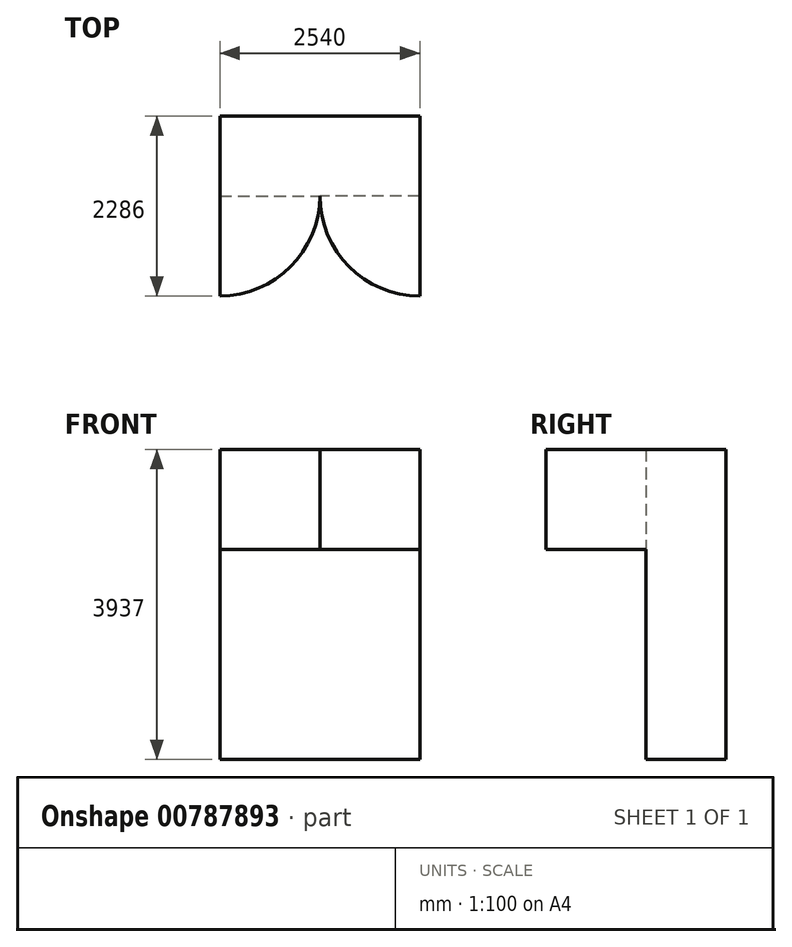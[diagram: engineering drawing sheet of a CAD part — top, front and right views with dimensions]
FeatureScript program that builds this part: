
annotation { "Feature Type Name" : "Feature", "Feature Type Description" : "" }
export const myFeature = defineFeature(function(context is Context, id is Id, definition is map)
    precondition{}
    {
        {
            var Q0;
            Q0=qCreatedBy(makeId("Top.planeOp"),FACE);
            var sketch = newSketch(context, id + "F0", { "sketchPlane" : qUnion([Q0])});
            skLineSegment(sketch, "E0.bottom", {"start": v(0, 0) * mm, "end": v(2540, 0) * mm});
            skLineSegment(sketch, "E0.top", {"start": v(0, 1016) * mm, "end": v(2540, 1016) * mm});
            skLineSegment(sketch, "E0.left", {"start": v(0, 0) * mm, "end": v(0, 1016) * mm});
            skLineSegment(sketch, "E0.right", {"start": v(2540, 0) * mm, "end": v(2540, 1016) * mm});
            skSolve(sketch);
        }
        {
            var Q0;
            Q0=makeQuery(id+"F0.imprint","IMPRINT",FACE,{"disambiguationData":[TD([[makeQuery(id+"F0.imprint","IMPRINT",EDGE,{"derivedFrom":sQuery(id+"F0.wireOp",EDGE,"E0.bottom")}),1.0]])]});
            extrude(context, id + "F1", {"entities" : qUnion([Q0]), "depth" : 3937 * mm, "offsetDistance" : 25.4 * mm});
        }
        {
            var Q0;
            Q0=makeQuery(id+"F1.opExtrude","SWEPT_FACE",FACE,{"disambiguationData":[OSD([sQuery(id+"F0.wireOp",EDGE,"E0.bottom")])]});
            var sketch = newSketch(context, id + "F2", { "sketchPlane" : qUnion([Q0])});
            skLineSegment(sketch, "E1", {"start": v(0, 2667) * mm, "end": v(1270, 2667) * mm});
            skSolve(sketch);
        }
        {
            var Q0;
            Q0=sQuery(id+"F2.wireOp",EDGE,"E1");
            var Q1;
            Q1=makeQuery(id+"F1.opExtrude","SWEPT_EDGE",EDGE,{"disambiguationData":[OSD([sQuery(id+"F0.wireOp",EDGE,"E0.bottom"),sQuery(id+"F0.wireOp",EDGE,"E0.left")])]});
            revolve(context, id + "F3", {"bodyType" : ToolBodyType.SURFACE, "surfaceOperationType" : NewSurfaceOperationType.NEW, "surfaceEntities" : qUnion([Q0]), "axis" : qUnion([Q1]), "revolveType" : RevolveType.TWO_DIRECTIONS, "angle" : 90 * degree, "angleBack" : 0 * degree});
        }
        {
            var Q0;
            Q0=makeQuery(id+"F3.opRevolve","SWEPT_FACE",FACE,{"disambiguationData":[OSD([sQuery(id+"F2.wireOp",EDGE,"E1")])]});
            extrude(context, id + "F4", {"entities" : qUnion([Q0]), "operationType" : NewBodyOperationType.ADD, "oppositeDirection" : true, "depth" : 1270 * mm, "offsetDistance" : 25.4 * mm});
        }
        {
            var Q0;
            Q0=makeQuery(id+"F1.opExtrude","SWEPT_FACE",FACE,{"disambiguationData":[OSD([sQuery(id+"F0.wireOp",EDGE,"E0.bottom")])]});
            var sketch = newSketch(context, id + "F5", { "sketchPlane" : qUnion([Q0])});
            skLineSegment(sketch, "E2", {"start": v(2540, 2667) * mm, "end": v(1270, 2667) * mm});
            skSolve(sketch);
        }
        {
            var Q0;
            Q0 = qSketchRegion(id + "F5", true);
            var Q1;
            Q1 = qConstructionFilter(qBodyType(qCreatedBy(id + "F5" ,EDGE), BodyType.WIRE), ConstructionObject.NO);
            var Q2;
            Q2=makeQuery(id+"F1.opExtrude","SWEPT_EDGE",EDGE,{"disambiguationData":[OSD([sQuery(id+"F0.wireOp",EDGE,"E0.bottom"),sQuery(id+"F0.wireOp",EDGE,"E0.right")])]});
            revolve(context, id + "F6", {"bodyType" : ToolBodyType.SURFACE, "surfaceOperationType" : NewSurfaceOperationType.NEW, "entities" : qUnion([Q0]), "surfaceEntities" : qUnion([Q1]), "axis" : qUnion([Q2]), "revolveType" : RevolveType.TWO_DIRECTIONS, "angle" : 0 * degree, "angleBack" : 270 * degree});
        }
        {
            var Q0;
            Q0=makeQuery(id+"F6.opRevolve","SWEPT_FACE",FACE,{"disambiguationData":[OSD([sQuery(id+"F5.wireOp",EDGE,"E2")])]});
            extrude(context, id + "F7", {"entities" : qUnion([Q0]), "operationType" : NewBodyOperationType.ADD, "oppositeDirection" : true, "depth" : 1270 * mm, "offsetDistance" : 25.4 * mm});
        }
    });
